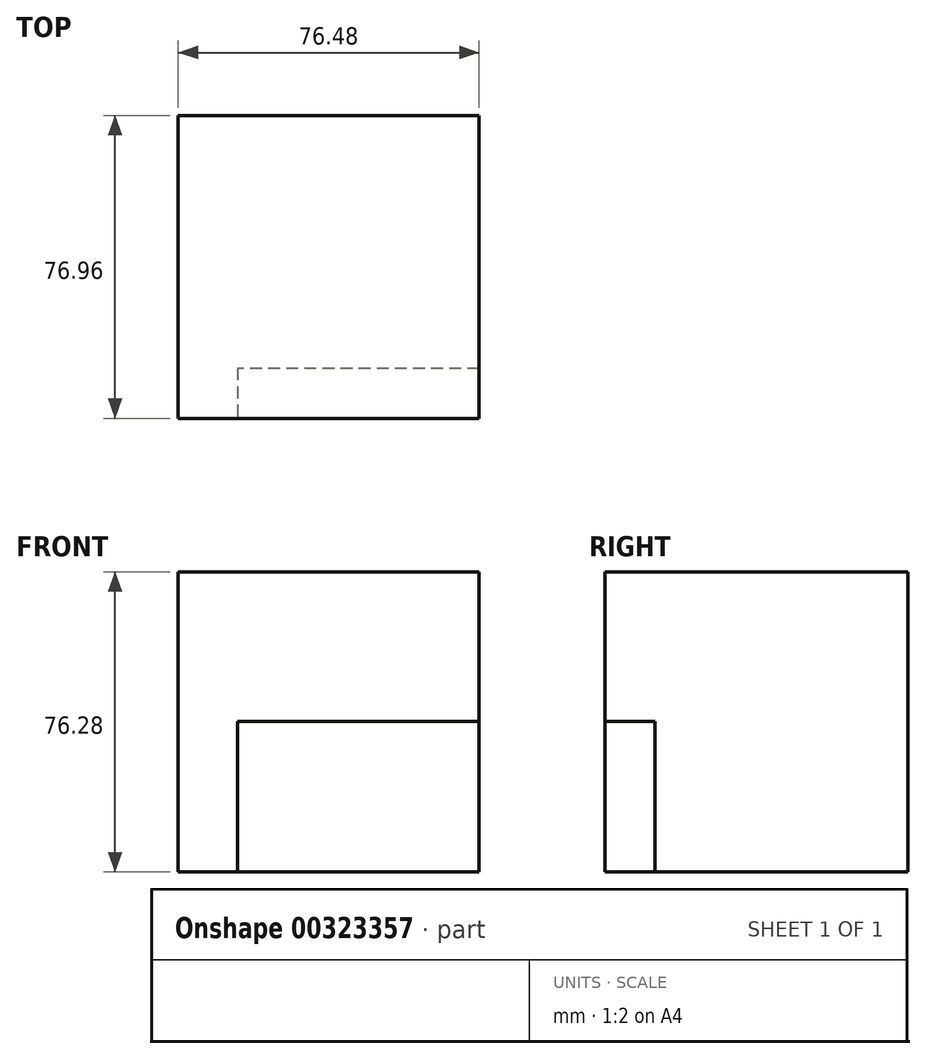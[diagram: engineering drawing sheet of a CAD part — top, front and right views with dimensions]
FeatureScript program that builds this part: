
annotation { "Feature Type Name" : "Feature", "Feature Type Description" : "" }
export const myFeature = defineFeature(function(context is Context, id is Id, definition is map)
    precondition{}
    {
        {
            var Q0;
            Q0=qCreatedBy(makeId("Front.planeOp"),FACE);
            var sketch = newSketch(context, id + "F0", { "sketchPlane" : qUnion([Q0])});
            skLineSegment(sketch, "E0", {"start": v(0, 0) * mm, "end": v(76.48, 0) * mm});
            skLineSegment(sketch, "E1", {"start": v(76.48, 0) * mm, "end": v(76.48, -76.28) * mm});
            skLineSegment(sketch, "E2", {"start": v(76.48, -76.28) * mm, "end": v(0, -76.28) * mm});
            skLineSegment(sketch, "E3", {"start": v(0, 0) * mm, "end": v(0, -76.28) * mm});
            skSolve(sketch);
        }
        {
            var Q0;
            Q0=makeQuery(id+"F0.imprint","IMPRINT",FACE,{"disambiguationData":[TD([[makeQuery(id+"F0.imprint","IMPRINT",EDGE,{"derivedFrom":sQuery(id+"F0.wireOp",EDGE,"E1")}),-1.0]])]});
            extrude(context, id + "F1", {"entities" : qUnion([Q0]), "depth" : 76.96 * mm});
        }
        {
            var Q0;
            Q0=makeQuery(id+"F1.opExtrude","CAP_FACE",FACE,{"disambiguationData":[OSD([sQuery(id+"F0.wireOp",EDGE,"E1"),sQuery(id+"F0.wireOp",EDGE,"E2"),sQuery(id+"F0.wireOp",EDGE,"E3"),sQuery(id+"F0.wireOp",EDGE,"E0")])],"isStart":false});
            var sketch = newSketch(context, id + "F2", { "sketchPlane" : qUnion([Q0])});
            skLineSegment(sketch, "E4", {"start": v(15.12, -76.28) * mm, "end": v(15.12, -38.02) * mm});
            skLineSegment(sketch, "E5", {"start": v(15.12, -38.02) * mm, "end": v(76.48, -38.02) * mm});
            skLineSegment(sketch, "E6", {"start": v(76.77, -37.38) * mm, "end": v(76.48, -76.28) * mm});
            skLineSegment(sketch, "E7", {"start": v(15.12, -76.28) * mm, "end": v(76.48, -76.28) * mm});
            skSolve(sketch);
        }
        {
            var Q0;
            Q0 = qSketchRegion(id + "F2", true);
            var Q1;
            Q1=makeQuery(id+"F2.imprint","IMPRINT",FACE,{"disambiguationData":[TD([[makeQuery(id+"F2.imprint","IMPRINT",EDGE,{"derivedFrom":sQuery(id+"F2.wireOp",EDGE,"E4")}),-1.0]])]});
            extrude(context, id + "F3", {"entities" : qUnion([Q0, Q1]), "operationType" : NewBodyOperationType.REMOVE, "oppositeDirection" : true, "depth" : 12.7 * mm});
        }
    });
